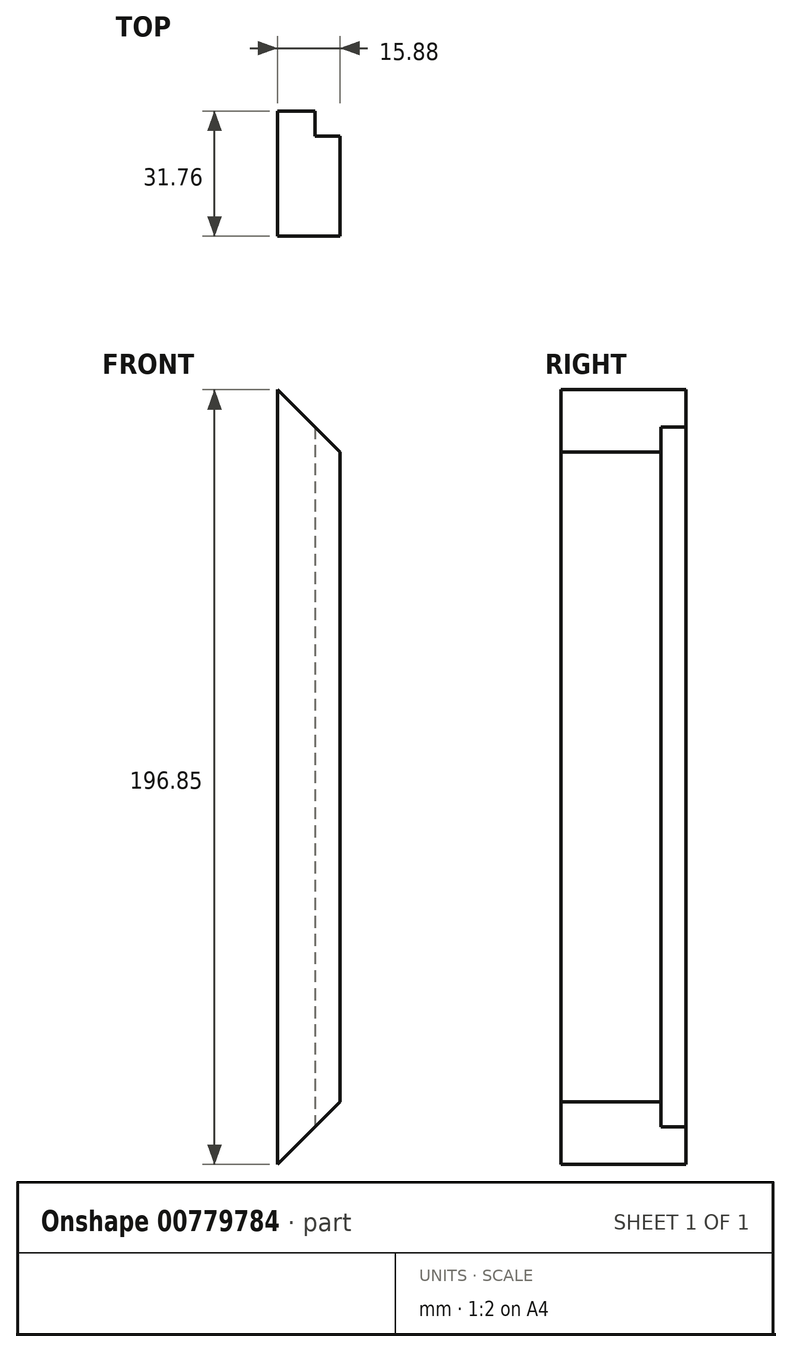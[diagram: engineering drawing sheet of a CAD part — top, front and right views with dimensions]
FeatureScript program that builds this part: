
annotation { "Feature Type Name" : "Feature", "Feature Type Description" : "" }
export const myFeature = defineFeature(function(context is Context, id is Id, definition is map)
    precondition{}
    {
        {
            var Q0;
            Q0=qCreatedBy(makeId("Top.planeOp"),FACE);
            var sketch = newSketch(context, id + "F0", { "sketchPlane" : qUnion([Q0])});
            skLineSegment(sketch, "E0.bottom", {"start": v(1.59, 15.88) * mm, "end": v(-7.94, 15.88) * mm});
            skLineSegment(sketch, "E0.top", {"start": v(7.94, -15.88) * mm, "end": v(-7.94, -15.88) * mm});
            skLineSegment(sketch, "E0.left", {"start": v(7.94, 9.53) * mm, "end": v(7.94, -15.88) * mm});
            skLineSegment(sketch, "E0.right", {"start": v(-7.94, 15.88) * mm, "end": v(-7.94, -15.88) * mm});
            skPoint(sketch, "E0.middle", {"position": v(0, 0) * mm});
            skLineSegment(sketch, "E1.top", {"start": v(7.94, 9.53) * mm, "end": v(1.59, 9.53) * mm});
            skLineSegment(sketch, "E1.right", {"start": v(1.59, 15.88) * mm, "end": v(1.59, 9.53) * mm});
            skPoint(sketch, "E2.orphan", {"position": v(7.94, 15.88) * mm});
            skSolve(sketch);
        }
        {
            var Q0;
            Q0 = qSketchRegion(id + "F0", true);
            extrude(context, id + "F1", {"entities" : qUnion([Q0]), "depth" : 196.85 * mm, "offsetDistance" : 25.4 * mm});
        }
        {
            var Q0;
            Q0=makeQuery(id+"F1.opExtrude","SWEPT_FACE",FACE,{"disambiguationData":[OSD([sQuery(id+"F0.wireOp",EDGE,"E0.top")])]});
            var sketch = newSketch(context, id + "F2", { "sketchPlane" : qUnion([Q0])});
            skLineSegment(sketch, "E3", {"start": v(-7.94, 196.85) * mm, "end": v(7.94, 180.98) * mm});
            skLineSegment(sketch, "E4", {"start": v(-7.94, 0) * mm, "end": v(7.94, 15.88) * mm});
            skSolve(sketch);
        }
        {
            var Q0;
            Q0 = qSketchRegion(id + "F2", true);
            var Q1;
            {var subQ0=sQuery(id+"F2.wireOp",EDGE,"E3");Q1=makeQuery(id+"F2.imprint","IMPRINT",FACE,{"disambiguationData":[TD([[makeQuery(id+"F2.imprint","IMPRINT",EDGE,{"derivedFrom":subQ0}),1.0]])]});}
            var Q2;
            {var subQ0=sQuery(id+"F2.wireOp",EDGE,"E4");Q2=makeQuery(id+"F2.imprint","IMPRINT",FACE,{"disambiguationData":[TD([[makeQuery(id+"F2.imprint","IMPRINT",EDGE,{"derivedFrom":subQ0}),-1.0]])]});}
            extrude(context, id + "F3", {"entities" : qUnion([Q0, Q1, Q2]), "operationType" : NewBodyOperationType.REMOVE, "endBound" : BoundingType.THROUGH_ALL, "oppositeDirection" : true, "depth" : 25.4 * mm, "offsetDistance" : 25.4 * mm});
        }
    });
